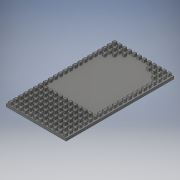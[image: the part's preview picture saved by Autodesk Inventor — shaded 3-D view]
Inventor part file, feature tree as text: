
AUTODESK INVENTOR PART (.ipt)
format: ipt  version: 2019.4 (Build 234330000, 330)  size: 934,400 bytes
history: native  units: in
note: dims shown in document units (in); Inventor stores cm internally (conversion verified against a paired STEP export)
features: extrude x2, sketch x2
ambient origin geometry x8: Origin, YZ Plane, XZ Plane, XY Plane, X Axis, Y Axis, Z Axis, Center Point
bodies: Solid1 (feature_tree)
feature tree (4):
  extrude  "Extrusion1"  Depth=1.7205in
  extrude  "Extrusion2"  Depth=0.0394in
  sketch  "Sketch1"  dims[d0=0.9567in d1=1.7205in]
  sketch  "Sketch2"  dims[d2=0.0394in d3=0.0in d4=0.0394in d5=0.0138in d6=0.0256in d7=8.6614in d9=0.0787in d10=4.7244in d12=0.0787in d15=0.0394in d16=0.0in]
